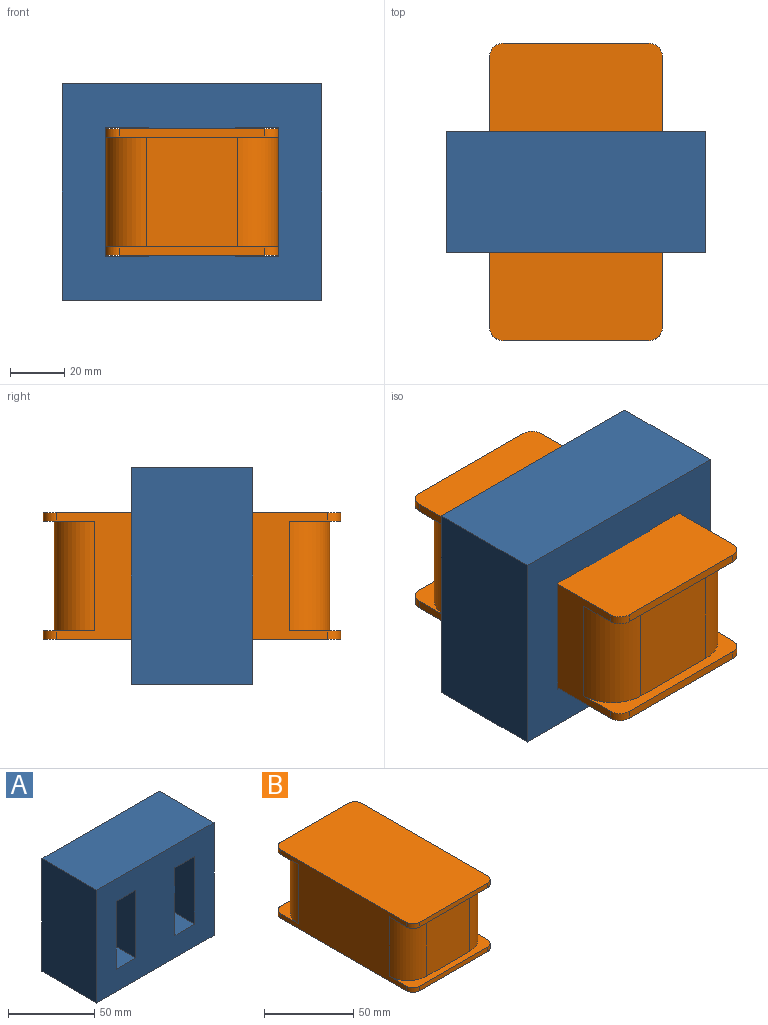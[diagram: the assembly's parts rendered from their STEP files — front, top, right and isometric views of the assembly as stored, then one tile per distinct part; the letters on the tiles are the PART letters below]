
ASSEMBLY  parts=2 mates=1
PART A: 14 faces, bbox 96x45x80 mm
  f0: plane 96x45mm, normal (0,0,-1), area 4320mm2, adj f1,f11,f12,f13
  f1: plane 80x45mm, normal (1,0,0), area 3600mm2, adj f0,f2,f12,f13
  f2: plane 96x45mm, normal (0,0,1), area 4320mm2, adj f1,f11,f12,f13
  f3: plane 48x45mm, normal (-1,0,0), area 2160mm2, adj f4,f9,f12,f13
  f4: plane 45x16mm, normal (0,0,1), area 720mm2, adj f3,f5,f12,f13
  f5: plane 48x45mm, normal (1,0,0), area 2160mm2, adj f4,f9,f12,f13
  f6: plane 48x45mm, normal (-1,0,0), area 2160mm2, adj f7,f10,f12,f13
  f7: plane 45x16mm, normal (0,0,1), area 720mm2, adj f6,f8,f12,f13
  f8: plane 48x45mm, normal (1,0,0), area 2160mm2, adj f7,f10,f12,f13
  f9: plane 45x16mm, normal (0,0,-1), area 720mm2, adj f3,f5,f12,f13
  f10: plane 45x16mm, normal (0,0,-1), area 720mm2, adj f6,f8,f12,f13
  f11: plane 80x45mm, normal (-1,0,0), area 3600mm2, adj f0,f2,f12,f13
  f12: plane 96x80mm, normal (0,-1,0), area 6144mm2, adj f0,f1,f2,f3,f4,f5,f6,f7
  f13: plane 96x80mm, normal (0,1,0), area 6144mm2, adj f0,f1,f2,f3,f4,f5,f6,f7
PART B: 26 faces, bbox 64x110x47 mm
  f0: plane 54x3.16mm, normal (0,-1,0), area 170.7mm2, adj f7,f11,f18,f21
  f1: plane 54x3.16mm, normal (0,1,0), area 170.7mm2, adj f6,f8,f23,f24
  f2: plane 100x47mm, normal (-1,0,0), area 3560.5mm2, adj f6,f7,f8,f9,f11,f13,f14,f15
  f3: plane 54x3.16mm, normal (0,-1,0), area 170.7mm2, adj f6,f13,f22,f25
  f4: plane 100x47mm, normal (1,0,0), area 3560.5mm2, adj f6,f7,f8,f9,f11,f13,f16,f17
  f5: plane 54x3.16mm, normal (0,1,0), area 170.7mm2, adj f7,f9,f19,f20
  f6: plane 110x64mm, normal (0,0,1), area 7018.5mm2, adj f1,f2,f3,f4,f22,f23,f24,f25
  f7: plane 110x64mm, normal (0,0,-1), area 7018.5mm2, adj f0,f2,f4,f5,f18,f19,f20,f21
  f8: plane 64x19.01mm, normal (0,0,-1), area 342.3mm2, adj f1,f2,f4,f10,f15,f16,f23,f24
  f9: plane 64x19.01mm, normal (0,0,1), area 342.3mm2, adj f2,f4,f5,f10,f15,f16,f19,f20
  f10: plane 40.68x34mm, normal (0,1,0), area 1383.1mm2, adj f8,f9,f15,f16
  f11: plane 64x19.01mm, normal (0,0,1), area 342.3mm2, adj f0,f2,f4,f12,f14,f17,f18,f21
  f12: plane 40.68x34mm, normal (0,-1,0), area 1383.1mm2, adj f11,f13,f14,f17
  f13: plane 64x19.01mm, normal (0,0,-1), area 342.3mm2, adj f2,f3,f4,f12,f14,f17,f22,f25
  f14: cylinder r=15mm len=40.68mm, axis (0,0,1), area 958.5mm2, adj f2,f11,f12,f13
  f15: cylinder r=15mm len=40.68mm, axis (0,0,-1), area 958.5mm2, adj f2,f8,f9,f10
  f16: cylinder r=15mm len=40.68mm, axis (0,0,-1), area 958.5mm2, adj f4,f8,f9,f10
  f17: cylinder r=15mm len=40.68mm, axis (0,0,1), area 958.5mm2, adj f4,f11,f12,f13
  f18: cylinder r=5mm len=5mm, axis (0,0,1), area 24.8mm2, adj f0,f4,f7,f11
  f19: cylinder r=5mm len=5mm, axis (0,0,-1), area 24.8mm2, adj f4,f5,f7,f9
  f20: cylinder r=5mm len=5mm, axis (0,0,1), area 24.8mm2, adj f2,f5,f7,f9
  f21: cylinder r=5mm len=5mm, axis (0,0,-1), area 24.8mm2, adj f0,f2,f7,f11
  f22: cylinder r=5mm len=5mm, axis (0,0,1), area 24.8mm2, adj f3,f4,f6,f13
  f23: cylinder r=5mm len=5mm, axis (0,0,-1), area 24.8mm2, adj f1,f4,f6,f8
  f24: cylinder r=5mm len=5mm, axis (0,0,1), area 24.8mm2, adj f1,f2,f6,f8
  f25: cylinder r=5mm len=5mm, axis (0,0,-1), area 24.8mm2, adj f2,f3,f6,f13
PLACE A t=(-19.9,52.2,0)mm
PLACE B t=(-19.9,29.7,-23.5)mm
MATE fastened B.f2 <-> A.f5  axis (-1,0,0) through (-51.9,29.7,0)mm
